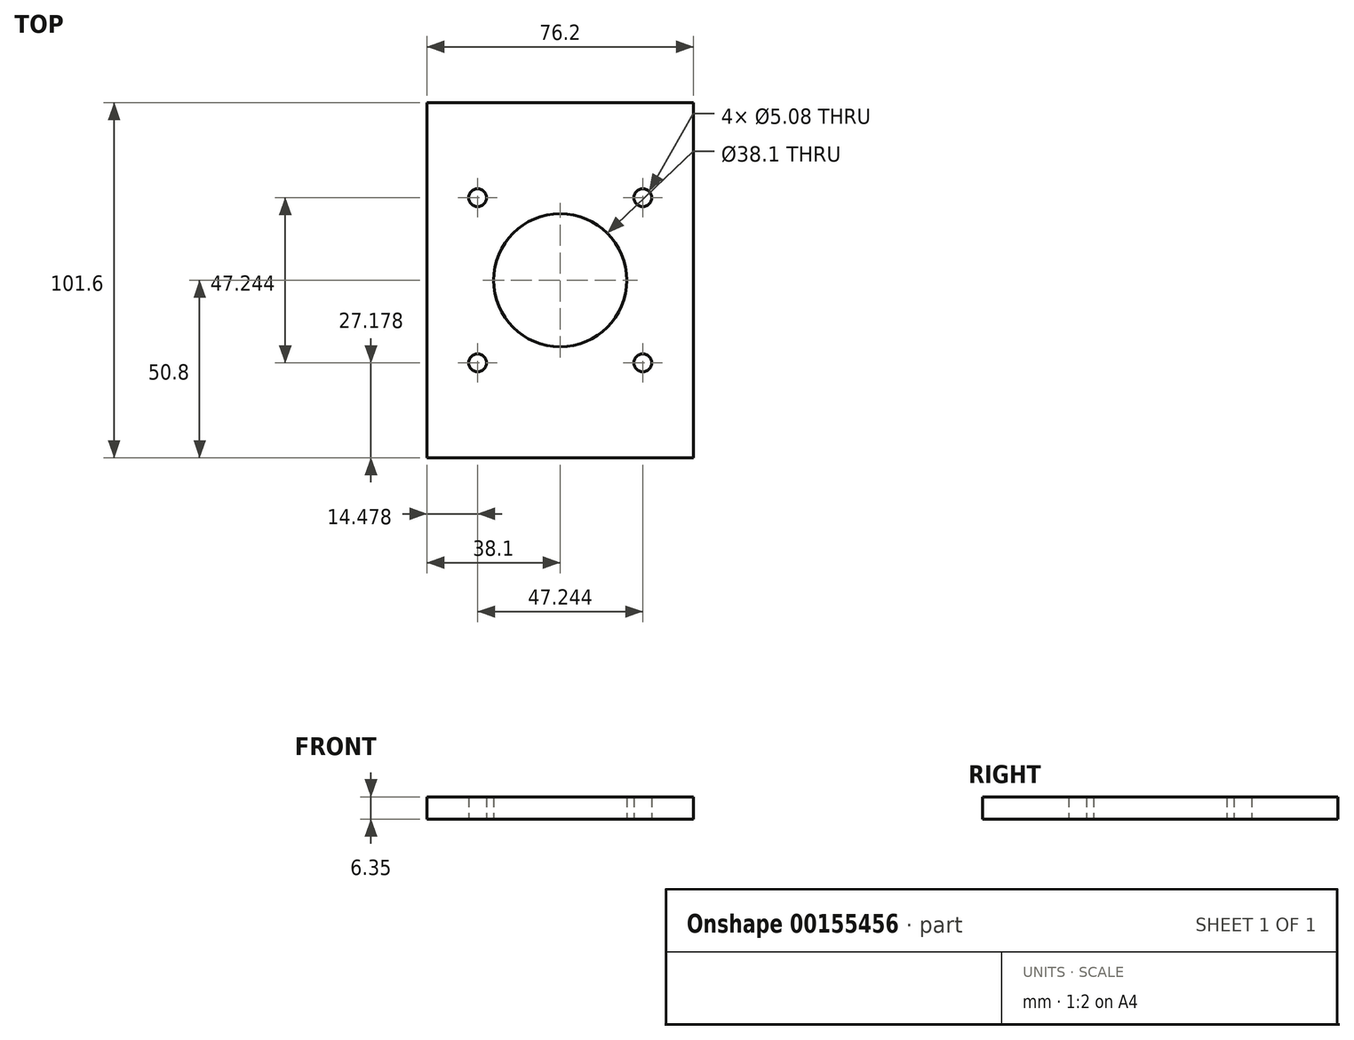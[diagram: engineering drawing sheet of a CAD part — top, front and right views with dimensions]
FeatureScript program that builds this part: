
annotation { "Feature Type Name" : "Feature", "Feature Type Description" : "" }
export const myFeature = defineFeature(function(context is Context, id is Id, definition is map)
    precondition{}
    {
        {
            var Q0;
            Q0=qCreatedBy(makeId("Top.planeOp"),FACE);
            var sketch = newSketch(context, id + "F0", { "sketchPlane" : qUnion([Q0])});
            skCircle(sketch, "E0.0", {"center": v(-23.62, -23.62) * mm, "radius": 2.54 * mm});
            skCircle(sketch, "E1.0", {"center": v(-23.62, 23.62) * mm, "radius": 2.54 * mm});
            skCircle(sketch, "E2.0", {"center": v(23.62, 23.62) * mm, "radius": 2.54 * mm});
            skCircle(sketch, "E3.0", {"center": v(23.62, -23.62) * mm, "radius": 2.54 * mm});
            skCircle(sketch, "E4.0", {"center": v(0, 0) * mm, "radius": 19.05 * mm});
            skLineSegment(sketch, "E5.bottom", {"start": v(-38.1, 50.8) * mm, "end": v(38.1, 50.8) * mm});
            skLineSegment(sketch, "E5.top", {"start": v(-38.1, -50.8) * mm, "end": v(38.1, -50.8) * mm});
            skLineSegment(sketch, "E5.left", {"start": v(-38.1, 50.8) * mm, "end": v(-38.1, -50.8) * mm});
            skLineSegment(sketch, "E5.right", {"start": v(38.1, 50.8) * mm, "end": v(38.1, -50.8) * mm});
            skSolve(sketch);
        }
        {
            var Q0;
            Q0 = qSketchRegion(id + "F0", true);
            extrude(context, id + "F1", {"entities" : qUnion([Q0]), "depth" : 6.35 * mm});
        }
    });
